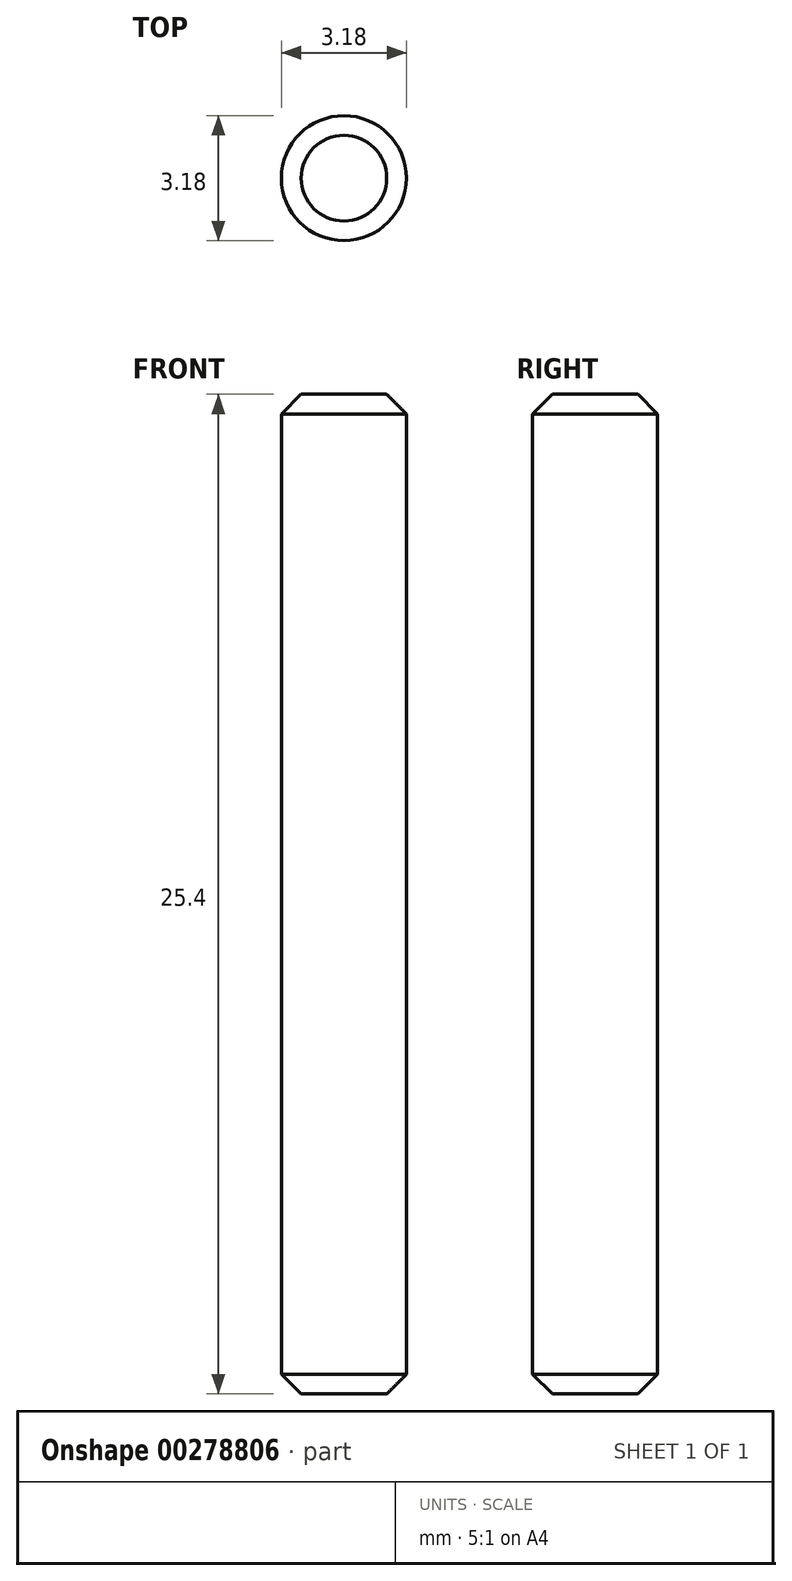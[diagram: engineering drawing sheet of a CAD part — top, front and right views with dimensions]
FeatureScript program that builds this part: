
annotation { "Feature Type Name" : "Feature", "Feature Type Description" : "" }
export const myFeature = defineFeature(function(context is Context, id is Id, definition is map)
    precondition{}
    {
        {
            var Q0;
            Q0=qCreatedBy(makeId("Top.planeOp"),FACE);
            var sketch = newSketch(context, id + "F0", { "sketchPlane" : qUnion([Q0])});
            skCircle(sketch, "E0", {"center": v(0, 0) * mm, "radius": 1.59 * mm});
            skSolve(sketch);
        }
        {
            var Q0;
            Q0=qSketchRegion(id+"F0",true);
            extrude(context, id + "F1", {"entities" : qUnion([Q0]), "depth" : 25.4 * mm});
        }
        {
            var Q0;
            Q0=makeQuery(id+"F1.opExtrude","CAP_EDGE",EDGE,{"disambiguationData":[OSD([sQuery(id+"F0.wireOp",EDGE,"E0")])],"isStart":false});
            var Q1;
            Q1=makeQuery(id+"F1.opExtrude","CAP_EDGE",EDGE,{"disambiguationData":[OSD([sQuery(id+"F0.wireOp",EDGE,"E0")])],"isStart":true});
            chamfer(context, id + "F2", {"entities" : qUnion([Q0, Q1]), "width" : 0.5 * mm, "tangentPropagation" : true});
        }
    });
